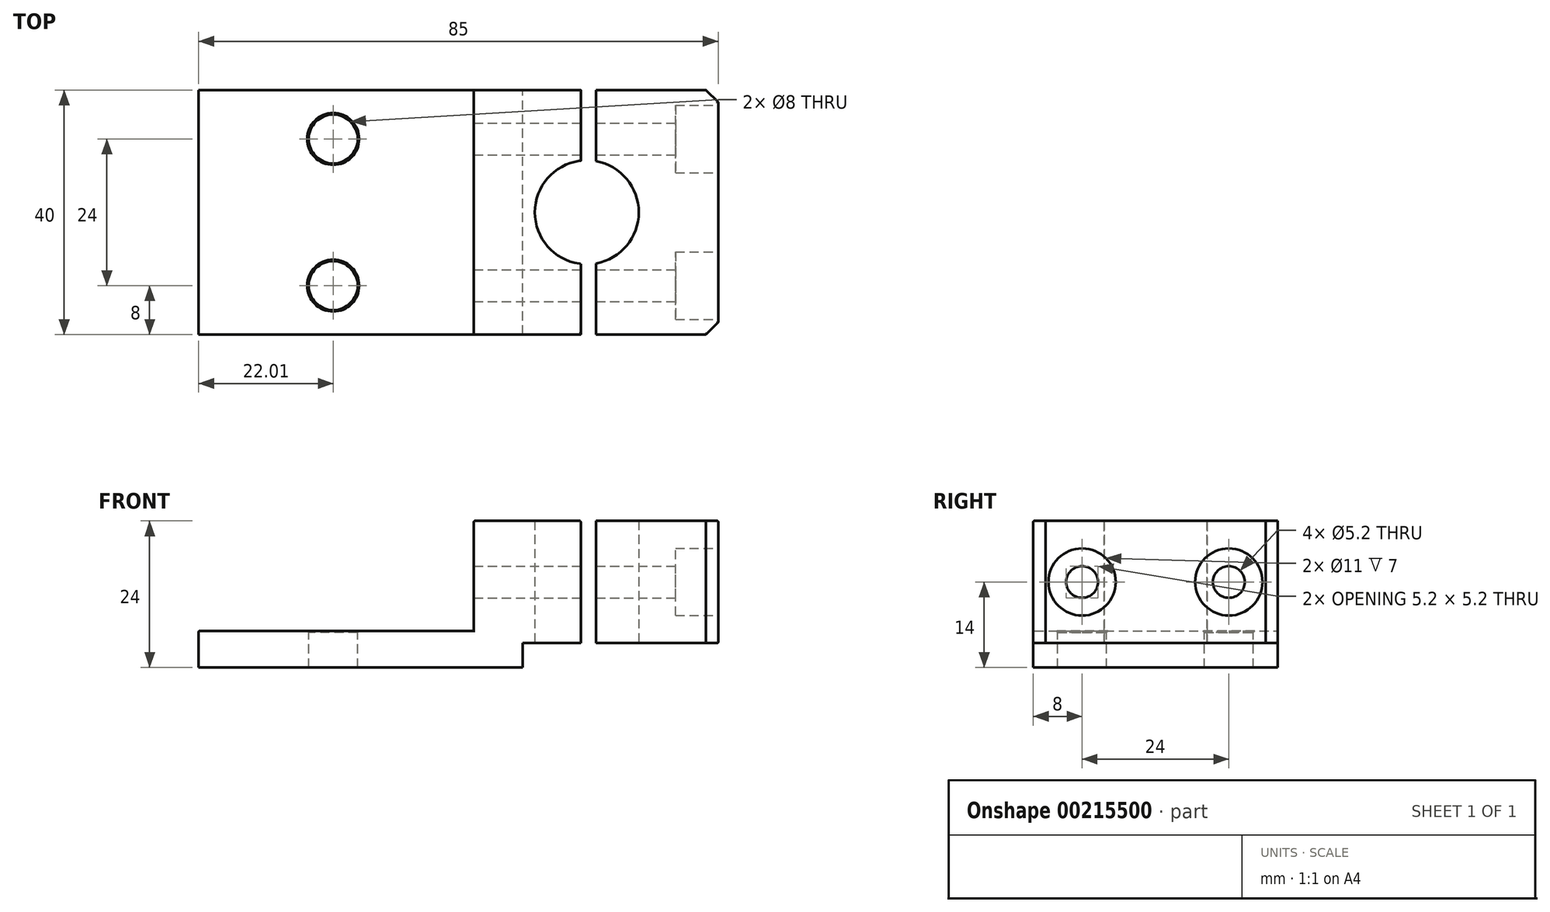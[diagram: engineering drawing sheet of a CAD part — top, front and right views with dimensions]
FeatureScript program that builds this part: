
annotation { "Feature Type Name" : "Feature", "Feature Type Description" : "" }
export const myFeature = defineFeature(function(context is Context, id is Id, definition is map)
    precondition{}
    {
        {
            var Q0;
            Q0=qCreatedBy(makeId("Front.planeOp"),FACE);
            var sketch = newSketch(context, id + "F0", { "sketchPlane" : qUnion([Q0])});
            skLineSegment(sketch, "E0", {"start": v(0, 0) * mm, "end": v(0, 6) * mm});
            skLineSegment(sketch, "E1", {"start": v(0, 6) * mm, "end": v(45, 6) * mm});
            skLineSegment(sketch, "E2", {"start": v(45, 6) * mm, "end": v(45, 24) * mm});
            skLineSegment(sketch, "E3", {"start": v(45, 24) * mm, "end": v(85, 24) * mm});
            skLineSegment(sketch, "E4", {"start": v(85, 24) * mm, "end": v(85, 4) * mm});
            skLineSegment(sketch, "E5", {"start": v(85, 4) * mm, "end": v(53, 4) * mm});
            skLineSegment(sketch, "E6", {"start": v(53, 4) * mm, "end": v(53, 0) * mm});
            skLineSegment(sketch, "E7", {"start": v(53, 0) * mm, "end": v(0, 0) * mm});
            skSolve(sketch);
        }
        {
            var Q0;
            Q0=makeQuery(id+"F0.imprint","IMPRINT",FACE,{"disambiguationData":[TD([[makeQuery(id+"F0.imprint","IMPRINT",EDGE,{"derivedFrom":sQuery(id+"F0.wireOp",EDGE,"E0")}),-1.0]])]});
            extrude(context, id + "F1", {"entities" : qUnion([Q0]), "depth" : 40 * mm});
        }
        {
            var Q0;
            Q0=qCreatedBy(makeId("Top.planeOp"),FACE);
            var sketch = newSketch(context, id + "F2", { "sketchPlane" : qUnion([Q0])});
            skPoint(sketch, "E8", {"position": v(63.5, -20) * mm});
            skPoint(sketch, "E9", {"position": v(66.84, 0) * mm});
            skPoint(sketch, "E10", {"position": v(22.5, -8) * mm});
            skPoint(sketch, "E11", {"position": v(22.5, -32) * mm});
            skSolve(sketch);
        }
        {
            var Q0;
            Q0=sQuery(id+"F2.wireOp",VERTEX,"E8");
            var Q1;
            Q1=makeQuery(id+"F1.opExtrude","SWEPT_BODY",BODY,{"disambiguationData":[OSD([sQuery(id+"F0.wireOp",EDGE,"E0"),sQuery(id+"F0.wireOp",EDGE,"E1"),sQuery(id+"F0.wireOp",EDGE,"E2"),sQuery(id+"F0.wireOp",EDGE,"E3"),sQuery(id+"F0.wireOp",EDGE,"E4"),sQuery(id+"F0.wireOp",EDGE,"E5"),sQuery(id+"F0.wireOp",EDGE,"E6"),sQuery(id+"F0.wireOp",EDGE,"E7")])]});
            hole(context, id + "F3", {"style" : HoleStyle.C_SINK, "endStyle" : HoleEndStyle.THROUGH, "oppositeDirection" : true, "holeDiameter" : 17 * mm, "cSinkDiameter" : 19 * mm, "cSinkAngle" : 82 * degree, "startFromSketch" : true, "locations" : qUnion([Q0]), "scope" : qUnion([Q1]), "isTappedThrough" : true});
        }
        {
            var Q0;
            Q0=makeQuery(id+"F1.opExtrude","SWEPT_FACE",FACE,{"disambiguationData":[OSD([sQuery(id+"F0.wireOp",EDGE,"E1")])]});
            var sketch = newSketch(context, id + "F4", { "sketchPlane" : qUnion([Q0])});
            skPoint(sketch, "E12", {"position": v(22, -8) * mm});
            skPoint(sketch, "E13", {"position": v(22, -32) * mm});
            skSolve(sketch);
        }
        {
            var Q0;
            Q0=sQuery(id+"F4.wireOp",VERTEX,"E12");
            var Q1;
            Q1=sQuery(id+"F4.wireOp",VERTEX,"E13");
            var Q2;
            Q2=makeQuery(id+"F1.opExtrude","SWEPT_BODY",BODY,{"disambiguationData":[OSD([sQuery(id+"F0.wireOp",EDGE,"E0"),sQuery(id+"F0.wireOp",EDGE,"E1"),sQuery(id+"F0.wireOp",EDGE,"E2"),sQuery(id+"F0.wireOp",EDGE,"E3"),sQuery(id+"F0.wireOp",EDGE,"E4"),sQuery(id+"F0.wireOp",EDGE,"E5"),sQuery(id+"F0.wireOp",EDGE,"E6"),sQuery(id+"F0.wireOp",EDGE,"E7")])]});
            hole(context, id + "F5", {"style" : HoleStyle.C_SINK, "endStyle" : HoleEndStyle.THROUGH, "holeDiameter" : 8 * mm, "cSinkDiameter" : 8.5 * mm, "cSinkAngle" : 82 * degree, "startFromSketch" : true, "locations" : qUnion([Q0, Q1]), "scope" : qUnion([Q2]), "isTappedThrough" : true});
        }
        {
            var Q0;
            Q0=makeQuery(id+"F1.opExtrude","SWEPT_FACE",FACE,{"disambiguationData":[OSD([sQuery(id+"F0.wireOp",EDGE,"E3")])]});
            var sketch = newSketch(context, id + "F6", { "sketchPlane" : qUnion([Q0])});
            skPoint(sketch, "E14", {"position": v(62.5, -40) * mm});
            skPoint(sketch, "E15", {"position": v(62.5, 0) * mm});
            skPoint(sketch, "E16", {"position": v(65, -40) * mm});
            skPoint(sketch, "E17", {"position": v(65, 0) * mm});
            skLineSegment(sketch, "E18", {"start": v(62.5, -40) * mm, "end": v(62.5, 0) * mm});
            skLineSegment(sketch, "E19", {"start": v(65, 0) * mm, "end": v(65, -40) * mm});
            skLineSegment(sketch, "E20", {"start": v(65, 0) * mm, "end": v(62.5, 0) * mm});
            skLineSegment(sketch, "E21", {"start": v(65, -40) * mm, "end": v(62.5, -40) * mm});
            skSolve(sketch);
        }
        {
            var Q0;
            {var subQ0=sQuery(id+"F6.wireOp",EDGE,"E21");Q0=makeQuery(id+"F6.imprint","IMPRINT",FACE,{"disambiguationData":[TD([[makeQuery(id+"F6.imprint","IMPRINT",EDGE,{"derivedFrom":subQ0}),1.0]])]});}
            var Q1;
            {var subQ0=sQuery(id+"F6.wireOp",EDGE,"E20");Q1=makeQuery(id+"F6.imprint","IMPRINT",FACE,{"disambiguationData":[TD([[makeQuery(id+"F6.imprint","IMPRINT",EDGE,{"derivedFrom":subQ0}),-1.0]])]});}
            var Q2;
            {var subQ0=sQuery(id+"F6.wireOp",EDGE,"E18");var subQ1=makeQuery(id+"F3.hole-0.boolean.opBoolean","INTERSECT",EDGE,{"derivedFrom":[makeQuery(id+"F1.opExtrude","SWEPT_FACE",FACE,{"disambiguationData":[OSD([sQuery(id+"F0.wireOp",EDGE,"E3")])]}),makeQuery(id+"F3.hole-0.opRevolve","SWEPT_FACE",FACE,{"disambiguationData":[OSD([sQuery(id+"F3.hole-0.sketch.wireOp",EDGE,"core_line_2")])]})]});var subQ2=makeQuery(id+"F6.imprint","INTERSECT",VERTEX,{"disambiguationData":[OD(0.0)],"derivedFrom":[subQ1,subQ0]});Q2=makeQuery(id+"F6.imprint","IMPRINT",FACE,{"disambiguationData":[TD([[makeQuery(id+"F6.imprint","IMPRINT",EDGE,{"disambiguationData":[TD([[subQ2,-1.0]])],"derivedFrom":subQ0}),-1.0]])]});}
            extrude(context, id + "F7", {"entities" : qUnion([Q0, Q1, Q2]), "operationType" : NewBodyOperationType.REMOVE, "endBound" : BoundingType.THROUGH_ALL, "oppositeDirection" : true, "depth" : 25 * mm});
        }
        {
            var Q0;
            Q0=makeQuery(id+"F1.opExtrude","SWEPT_FACE",FACE,{"disambiguationData":[OSD([sQuery(id+"F0.wireOp",EDGE,"E4")])]});
            var sketch = newSketch(context, id + "F8", { "sketchPlane" : qUnion([Q0])});
            skPoint(sketch, "E22", {"position": v(-8, 14) * mm});
            skPoint(sketch, "E22.positionSnap0", {"position": v(0, 14) * mm});
            skPoint(sketch, "E23", {"position": v(-32, 14) * mm});
            skSolve(sketch);
        }
        {
            var Q0;
            Q0=sQuery(id+"F8.wireOp",VERTEX,"E22");
            var Q1;
            Q1=sQuery(id+"F8.wireOp",VERTEX,"E23");
            var Q2;
            Q2=makeQuery(id+"F7.boolean.opBoolean","SPLIT",BODY,{"disambiguationData":[OD(0.0)],"derivedFrom":makeQuery(id+"F1.opExtrude","SWEPT_BODY",BODY,{"disambiguationData":[OSD([sQuery(id+"F0.wireOp",EDGE,"E0"),sQuery(id+"F0.wireOp",EDGE,"E1"),sQuery(id+"F0.wireOp",EDGE,"E2"),sQuery(id+"F0.wireOp",EDGE,"E3"),sQuery(id+"F0.wireOp",EDGE,"E4"),sQuery(id+"F0.wireOp",EDGE,"E5"),sQuery(id+"F0.wireOp",EDGE,"E6"),sQuery(id+"F0.wireOp",EDGE,"E7")])]})});
            var Q3;
            Q3=makeQuery(id+"F7.boolean.opBoolean","SPLIT",BODY,{"disambiguationData":[OD(1.0)],"derivedFrom":makeQuery(id+"F1.opExtrude","SWEPT_BODY",BODY,{"disambiguationData":[OSD([sQuery(id+"F0.wireOp",EDGE,"E0"),sQuery(id+"F0.wireOp",EDGE,"E1"),sQuery(id+"F0.wireOp",EDGE,"E2"),sQuery(id+"F0.wireOp",EDGE,"E3"),sQuery(id+"F0.wireOp",EDGE,"E4"),sQuery(id+"F0.wireOp",EDGE,"E5"),sQuery(id+"F0.wireOp",EDGE,"E6"),sQuery(id+"F0.wireOp",EDGE,"E7")])]})});
            hole(context, id + "F9", {"style" : HoleStyle.C_BORE, "endStyle" : HoleEndStyle.BLIND, "holeDiameter" : 5.2 * mm, "cBoreDiameter" : 11 * mm, "cBoreDepth" : 7 * mm, "holeDepth" : 45 * mm, "startFromSketch" : true, "locations" : qUnion([Q0, Q1]), "scope" : qUnion([Q2, Q3])});
        }
        {
            var Q0;
            Q0=makeQuery(id+"F1.opExtrude","CAP_EDGE",EDGE,{"disambiguationData":[OSD([sQuery(id+"F0.wireOp",EDGE,"E4")])],"isStart":false});
            var Q1;
            Q1=makeQuery(id+"F1.opExtrude","CAP_EDGE",EDGE,{"disambiguationData":[OSD([sQuery(id+"F0.wireOp",EDGE,"E4")])],"isStart":true});
            chamfer(context, id + "F10", {"entities" : qUnion([Q0, Q1]), "width" : 2 * mm, "tangentPropagation" : true});
        }
        {
            var Q0;
            {var subQ0=sQuery(id+"F0.wireOp",EDGE,"E4");var subQ4=sQuery(id+"F0.wireOp",EDGE,"E3");Q0=makeQuery(id+"F10.opChamfer","BLEND_EDGE",EDGE,{"blendedFrom":[makeQuery(id+"F1.opExtrude","CAP_EDGE",EDGE,{"disambiguationData":[OSD([subQ0])],"isStart":true}),makeQuery(id+"F7.boolean.opBoolean","SPLIT",FACE,{"disambiguationData":[TD([makeQuery(id+"F1.opExtrude","SWEPT_FACE",FACE,{"disambiguationData":[OSD([subQ0])]})])],"derivedFrom":makeQuery(id+"F1.opExtrude","SWEPT_FACE",FACE,{"disambiguationData":[OSD([subQ4])]})})],"blendedInto":[makeQuery(id+"F7.boolean.opBoolean","SPLIT",FACE,{"disambiguationData":[TD([makeQuery(id+"F1.opExtrude","SWEPT_FACE",FACE,{"disambiguationData":[OSD([subQ0])]})])],"derivedFrom":makeQuery(id+"F1.opExtrude","SWEPT_FACE",FACE,{"disambiguationData":[OSD([subQ4])]})})]});}
            var Q1;
            Q1=makeQuery(id+"F1.opExtrude","SWEPT_EDGE",EDGE,{"disambiguationData":[OSD([sQuery(id+"F0.wireOp",EDGE,"E3"),sQuery(id+"F0.wireOp",EDGE,"E4")])]});
            var Q2;
            {var subQ0=sQuery(id+"F0.wireOp",EDGE,"E4");var subQ4=sQuery(id+"F0.wireOp",EDGE,"E3");Q2=makeQuery(id+"F10.opChamfer","BLEND_EDGE",EDGE,{"blendedFrom":[makeQuery(id+"F1.opExtrude","CAP_EDGE",EDGE,{"disambiguationData":[OSD([subQ0])],"isStart":false}),makeQuery(id+"F7.boolean.opBoolean","SPLIT",FACE,{"disambiguationData":[TD([makeQuery(id+"F1.opExtrude","SWEPT_FACE",FACE,{"disambiguationData":[OSD([subQ0])]})])],"derivedFrom":makeQuery(id+"F1.opExtrude","SWEPT_FACE",FACE,{"disambiguationData":[OSD([subQ4])]})})],"blendedInto":[makeQuery(id+"F7.boolean.opBoolean","SPLIT",FACE,{"disambiguationData":[TD([makeQuery(id+"F1.opExtrude","SWEPT_FACE",FACE,{"disambiguationData":[OSD([subQ0])]})])],"derivedFrom":makeQuery(id+"F1.opExtrude","SWEPT_FACE",FACE,{"disambiguationData":[OSD([subQ4])]})})]});}
            var Q3;
            {var subQ0=sQuery(id+"F0.wireOp",EDGE,"E3");var subQ1=sQuery(id+"F6.wireOp",EDGE,"E18");Q3=makeQuery(id+"F7.boolean.opBoolean","COPY",EDGE,{"disambiguationData":[TD([makeQuery(id+"F1.opExtrude","CAP_FACE",FACE,{"disambiguationData":[OSD([sQuery(id+"F0.wireOp",EDGE,"E0"),sQuery(id+"F0.wireOp",EDGE,"E1"),sQuery(id+"F0.wireOp",EDGE,"E2"),subQ0,sQuery(id+"F0.wireOp",EDGE,"E4"),sQuery(id+"F0.wireOp",EDGE,"E5"),sQuery(id+"F0.wireOp",EDGE,"E6"),sQuery(id+"F0.wireOp",EDGE,"E7")])],"isStart":false})])],"derivedFrom":makeQuery(id+"F7.opExtrude","CAP_EDGE",EDGE,{"disambiguationData":[OSD([subQ1])],"isStart":true})});}
            var Q4;
            {var subQ0=makeQuery(id+"F1.opExtrude","SWEPT_FACE",FACE,{"disambiguationData":[OSD([sQuery(id+"F0.wireOp",EDGE,"E3")])]});var subQ1=makeQuery(id+"F3.hole-0.opRevolve","SWEPT_FACE",FACE,{"disambiguationData":[OSD([sQuery(id+"F3.hole-0.sketch.wireOp",EDGE,"core_line_2")])]});Q4=makeQuery(id+"F7.boolean.opBoolean","SPLIT",EDGE,{"disambiguationData":[TD([makeQuery(id+"F7.opExtrude","SWEPT_FACE",FACE,{"disambiguationData":[OSD([sQuery(id+"F6.wireOp",EDGE,"E19")])]})])],"derivedFrom":makeQuery(id+"F3.hole-0.boolean.opBoolean","INTERSECT",EDGE,{"derivedFrom":[subQ0,subQ1]})});}
            var Q5;
            {var subQ0=makeQuery(id+"F1.opExtrude","SWEPT_FACE",FACE,{"disambiguationData":[OSD([sQuery(id+"F0.wireOp",EDGE,"E3")])]});var subQ1=makeQuery(id+"F3.hole-0.opRevolve","SWEPT_FACE",FACE,{"disambiguationData":[OSD([sQuery(id+"F3.hole-0.sketch.wireOp",EDGE,"core_line_2")])]});Q5=makeQuery(id+"F7.boolean.opBoolean","SPLIT",EDGE,{"disambiguationData":[TD([makeQuery(id+"F7.opExtrude","SWEPT_FACE",FACE,{"disambiguationData":[OSD([sQuery(id+"F6.wireOp",EDGE,"E18")])]})])],"derivedFrom":makeQuery(id+"F3.hole-0.boolean.opBoolean","INTERSECT",EDGE,{"derivedFrom":[subQ0,subQ1]})});}
            var Q6;
            {var subQ0=sQuery(id+"F0.wireOp",EDGE,"E3");var subQ1=sQuery(id+"F6.wireOp",EDGE,"E18");Q6=makeQuery(id+"F7.boolean.opBoolean","COPY",EDGE,{"disambiguationData":[TD([makeQuery(id+"F1.opExtrude","CAP_FACE",FACE,{"disambiguationData":[OSD([sQuery(id+"F0.wireOp",EDGE,"E0"),sQuery(id+"F0.wireOp",EDGE,"E1"),sQuery(id+"F0.wireOp",EDGE,"E2"),subQ0,sQuery(id+"F0.wireOp",EDGE,"E4"),sQuery(id+"F0.wireOp",EDGE,"E5"),sQuery(id+"F0.wireOp",EDGE,"E6"),sQuery(id+"F0.wireOp",EDGE,"E7")])],"isStart":true})])],"derivedFrom":makeQuery(id+"F7.opExtrude","CAP_EDGE",EDGE,{"disambiguationData":[OSD([subQ1])],"isStart":true})});}
            var Q7;
            {var subQ0=sQuery(id+"F0.wireOp",EDGE,"E3");var subQ1=sQuery(id+"F6.wireOp",EDGE,"E19");Q7=makeQuery(id+"F7.boolean.opBoolean","COPY",EDGE,{"disambiguationData":[TD([makeQuery(id+"F1.opExtrude","CAP_FACE",FACE,{"disambiguationData":[OSD([sQuery(id+"F0.wireOp",EDGE,"E0"),sQuery(id+"F0.wireOp",EDGE,"E1"),sQuery(id+"F0.wireOp",EDGE,"E2"),subQ0,sQuery(id+"F0.wireOp",EDGE,"E4"),sQuery(id+"F0.wireOp",EDGE,"E5"),sQuery(id+"F0.wireOp",EDGE,"E6"),sQuery(id+"F0.wireOp",EDGE,"E7")])],"isStart":true})])],"derivedFrom":makeQuery(id+"F7.opExtrude","CAP_EDGE",EDGE,{"disambiguationData":[OSD([subQ1])],"isStart":true})});}
            var Q8;
            {var subQ0=sQuery(id+"F0.wireOp",EDGE,"E3");var subQ1=sQuery(id+"F6.wireOp",EDGE,"E19");Q8=makeQuery(id+"F7.boolean.opBoolean","COPY",EDGE,{"disambiguationData":[TD([makeQuery(id+"F1.opExtrude","CAP_FACE",FACE,{"disambiguationData":[OSD([sQuery(id+"F0.wireOp",EDGE,"E0"),sQuery(id+"F0.wireOp",EDGE,"E1"),sQuery(id+"F0.wireOp",EDGE,"E2"),subQ0,sQuery(id+"F0.wireOp",EDGE,"E4"),sQuery(id+"F0.wireOp",EDGE,"E5"),sQuery(id+"F0.wireOp",EDGE,"E6"),sQuery(id+"F0.wireOp",EDGE,"E7")])],"isStart":false})])],"derivedFrom":makeQuery(id+"F7.opExtrude","CAP_EDGE",EDGE,{"disambiguationData":[OSD([subQ1])],"isStart":true})});}
            var Q9;
            {var subQ0=sQuery(id+"F0.wireOp",EDGE,"E4");var subQ1=sQuery(id+"F0.wireOp",EDGE,"E3");Q9=makeQuery(id+"F7.boolean.opBoolean","SPLIT",EDGE,{"disambiguationData":[TD([makeQuery(id+"F1.opExtrude","SWEPT_FACE",FACE,{"disambiguationData":[OSD([subQ0])]})])],"derivedFrom":makeQuery(id+"F1.opExtrude","CAP_EDGE",EDGE,{"disambiguationData":[OSD([subQ1])],"isStart":false})});}
            var Q10;
            Q10=makeQuery(id+"F1.opExtrude","SWEPT_EDGE",EDGE,{"disambiguationData":[OSD([sQuery(id+"F0.wireOp",EDGE,"E4"),sQuery(id+"F0.wireOp",EDGE,"E5")])]});
            var Q11;
            {var subQ0=sQuery(id+"F0.wireOp",EDGE,"E5");var subQ1=sQuery(id+"F0.wireOp",EDGE,"E4");Q11=makeQuery(id+"F7.boolean.opBoolean","SPLIT",EDGE,{"disambiguationData":[TD([makeQuery(id+"F1.opExtrude","SWEPT_FACE",FACE,{"disambiguationData":[OSD([subQ1])]})])],"derivedFrom":makeQuery(id+"F1.opExtrude","CAP_EDGE",EDGE,{"disambiguationData":[OSD([subQ0])],"isStart":false})});}
            var Q12;
            Q12=makeQuery(id+"F1.opExtrude","CAP_EDGE",EDGE,{"disambiguationData":[OSD([sQuery(id+"F0.wireOp",EDGE,"E1")])],"isStart":true});
            var Q13;
            Q13=makeQuery(id+"F1.opExtrude","SWEPT_EDGE",EDGE,{"disambiguationData":[OSD([sQuery(id+"F0.wireOp",EDGE,"E0"),sQuery(id+"F0.wireOp",EDGE,"E1")])]});
            var Q14;
            {var subQ0=sQuery(id+"F0.wireOp",EDGE,"E3");var subQ1=sQuery(id+"F0.wireOp",EDGE,"E2");Q14=makeQuery(id+"F7.boolean.opBoolean","SPLIT",EDGE,{"disambiguationData":[TD([makeQuery(id+"F1.opExtrude","SWEPT_FACE",FACE,{"disambiguationData":[OSD([subQ1])]})])],"derivedFrom":makeQuery(id+"F1.opExtrude","CAP_EDGE",EDGE,{"disambiguationData":[OSD([subQ0])],"isStart":false})});}
            var Q15;
            Q15=makeQuery(id+"F1.opExtrude","SWEPT_EDGE",EDGE,{"disambiguationData":[OSD([sQuery(id+"F0.wireOp",EDGE,"E2"),sQuery(id+"F0.wireOp",EDGE,"E3")])]});
            var Q16;
            Q16=makeQuery(id+"F1.opExtrude","CAP_EDGE",EDGE,{"disambiguationData":[OSD([sQuery(id+"F0.wireOp",EDGE,"E1")])],"isStart":false});
            var Q17;
            {var subQ0=sQuery(id+"F0.wireOp",EDGE,"E4");var subQ3=sQuery(id+"F0.wireOp",EDGE,"E5");Q17=makeQuery(id+"F10.opChamfer","BLEND_EDGE",EDGE,{"blendedFrom":[makeQuery(id+"F1.opExtrude","CAP_EDGE",EDGE,{"disambiguationData":[OSD([subQ0])],"isStart":true}),makeQuery(id+"F7.boolean.opBoolean","SPLIT",FACE,{"disambiguationData":[TD([makeQuery(id+"F1.opExtrude","SWEPT_FACE",FACE,{"disambiguationData":[OSD([subQ0])]})])],"derivedFrom":makeQuery(id+"F1.opExtrude","SWEPT_FACE",FACE,{"disambiguationData":[OSD([subQ3])]})})],"blendedInto":[makeQuery(id+"F7.boolean.opBoolean","SPLIT",FACE,{"disambiguationData":[TD([makeQuery(id+"F1.opExtrude","SWEPT_FACE",FACE,{"disambiguationData":[OSD([subQ0])]})])],"derivedFrom":makeQuery(id+"F1.opExtrude","SWEPT_FACE",FACE,{"disambiguationData":[OSD([subQ3])]})})]});}
            var Q18;
            Q18=makeQuery(id+"F9.hole-0.boolean.opBoolean","COPY",EDGE,{"derivedFrom":makeQuery(id+"F9.hole-0.opRevolve","SWEPT_EDGE",EDGE,{"disambiguationData":[OSD([sQuery(id+"F9.hole-0.sketch.wireOp",EDGE,"cbore_start_line_1"),sQuery(id+"F9.hole-0.sketch.wireOp",EDGE,"core_line_2")])]})});
            fillet(context, id + "F11", {"entities" : qUnion([Q0, Q1, Q2, Q3, Q4, Q5, Q6, Q7, Q8, Q9, Q10, Q11, Q12, Q13, Q14, Q15, Q16, Q17, Q18]), "radius" : .2 * mm, "tangentPropagation" : true, "allowEdgeOverflow" : false});
        }
    });
